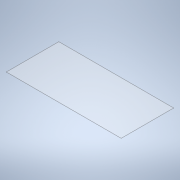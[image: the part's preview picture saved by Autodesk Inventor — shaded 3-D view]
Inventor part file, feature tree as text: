
AUTODESK INVENTOR PART (.ipt)
format: ipt  version: 2020 (Build 240168000, 168)  size: 93,696 bytes
history: native  units: in
note: dims shown in document units (in); Inventor stores cm internally (conversion verified against a paired STEP export)
features: extrude x1, sketch x1
ambient origin geometry x8: Origin, YZ Plane, XZ Plane, XY Plane, X Axis, Y Axis, Z Axis, Center Point
bodies: Solid1 (feature_tree)
feature tree (2):
  extrude  "Extrusion1"  Depth=8.0in
  sketch  "Sketch1"  dims[d0=17.5in d1=8.0in d2=0.04in d3=0.0in]
